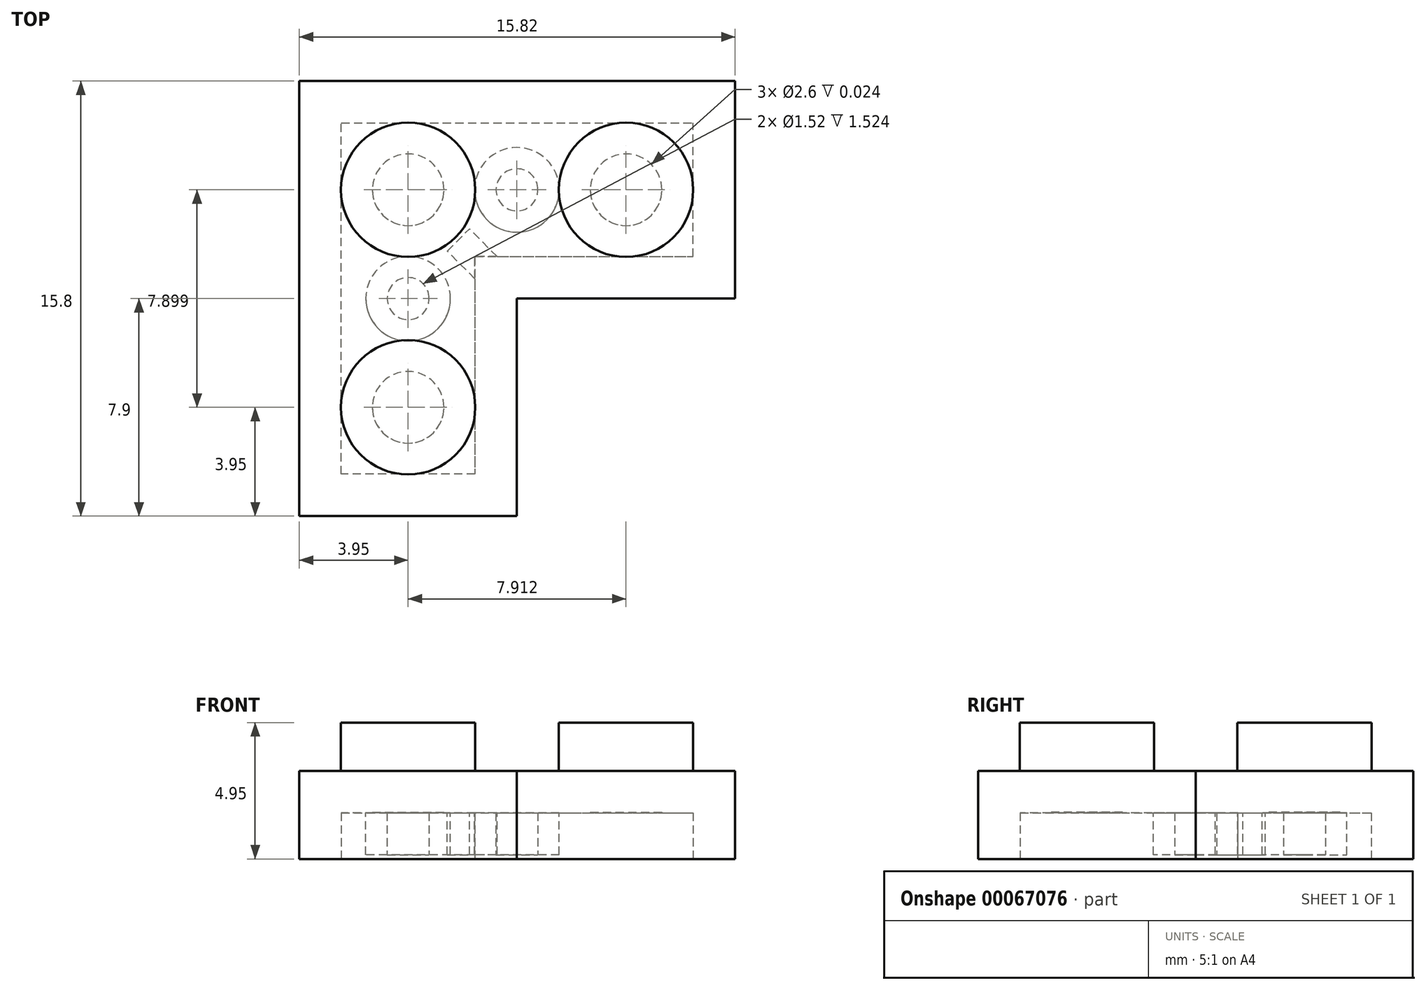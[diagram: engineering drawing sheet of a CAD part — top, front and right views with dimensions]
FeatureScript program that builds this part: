
annotation { "Feature Type Name" : "Feature", "Feature Type Description" : "" }
export const myFeature = defineFeature(function(context is Context, id is Id, definition is map)
    precondition{}
    {
        {
            var Q0;
            Q0=qCreatedBy(makeId("Top.planeOp"),FACE);
            var sketch = newSketch(context, id + "F0", { "sketchPlane" : qUnion([Q0])});
            skLineSegment(sketch, "E0.top", {"start": v(0, -7.9) * mm, "end": v(-7.9, -7.9) * mm});
            skLineSegment(sketch, "E0.left", {"start": v(0, 0) * mm, "end": v(0, -7.9) * mm});
            skLineSegment(sketch, "E0.right", {"start": v(-7.9, 0) * mm, "end": v(-7.9, -7.9) * mm});
            skLineSegment(sketch, "E1.bottom", {"start": v(0, 0) * mm, "end": v(7.92, 0) * mm});
            skLineSegment(sketch, "E1.top", {"start": v(-7.9, 7.9) * mm, "end": v(7.92, 7.9) * mm});
            skLineSegment(sketch, "E1.left", {"start": v(-7.9, 0) * mm, "end": v(-7.9, 7.9) * mm});
            skLineSegment(sketch, "E1.right", {"start": v(7.92, 0) * mm, "end": v(7.92, 7.9) * mm});
            skSolve(sketch);
        }
        {
            var Q0;
            Q0 = qSketchRegion(id + "F0", true);
            extrude(context, id + "F1", {"entities" : qUnion([Q0]), "depth" : 3.2 * mm});
        }
        {
            var Q0;
            Q0=makeQuery(id+"F1.opExtrude","CAP_FACE",FACE,{"disambiguationData":[OSD([sQuery(id+"F0.wireOp",EDGE,"E0.top"),sQuery(id+"F0.wireOp",EDGE,"E0.left"),sQuery(id+"F0.wireOp",EDGE,"E0.right"),sQuery(id+"F0.wireOp",EDGE,"E1.bottom"),sQuery(id+"F0.wireOp",EDGE,"E1.top"),sQuery(id+"F0.wireOp",EDGE,"E1.left"),sQuery(id+"F0.wireOp",EDGE,"E1.right")])],"isStart":true});
            shell(context, id + "F2", {"entities" : qUnion([Q0]), "thickness" : 1.52 * mm});
        }
        {
            var Q0;
            Q0=makeQuery(id+"F1.opExtrude","CAP_FACE",FACE,{"disambiguationData":[OSD([sQuery(id+"F0.wireOp",EDGE,"E0.top"),sQuery(id+"F0.wireOp",EDGE,"E0.left"),sQuery(id+"F0.wireOp",EDGE,"E0.right"),sQuery(id+"F0.wireOp",EDGE,"E1.bottom"),sQuery(id+"F0.wireOp",EDGE,"E1.top"),sQuery(id+"F0.wireOp",EDGE,"E1.left"),sQuery(id+"F0.wireOp",EDGE,"E1.right")])],"isStart":false});
            var sketch = newSketch(context, id + "F3", { "sketchPlane" : qUnion([Q0])});
            skCircle(sketch, "E2", {"center": v(3.96, 3.95) * mm, "radius": 2.44 * mm});
            skCircle(sketch, "E3", {"center": v(-3.95, 3.95) * mm, "radius": 2.44 * mm});
            skCircle(sketch, "E4", {"center": v(-3.95, -3.95) * mm, "radius": 2.44 * mm});
            skSolve(sketch);
        }
        {
            var Q0;
            Q0 = qSketchRegion(id + "F3", true);
            extrude(context, id + "F4", {"entities" : qUnion([Q0]), "operationType" : NewBodyOperationType.ADD, "depth" : 1.75 * mm});
        }
        {
            var Q0;
            Q0=makeQuery(id+"F1.opExtrude","CAP_FACE",FACE,{"disambiguationData":[OSD([sQuery(id+"F0.wireOp",EDGE,"E0.top"),sQuery(id+"F0.wireOp",EDGE,"E0.left"),sQuery(id+"F0.wireOp",EDGE,"E0.right"),sQuery(id+"F0.wireOp",EDGE,"E1.bottom"),sQuery(id+"F0.wireOp",EDGE,"E1.top"),sQuery(id+"F0.wireOp",EDGE,"E1.left"),sQuery(id+"F0.wireOp",EDGE,"E1.right")])],"isStart":true});
            var sketch = newSketch(context, id + "F5", { "sketchPlane" : qUnion([Q0])});
            skCircle(sketch, "E5", {"center": v(-3.95, 3.95) * mm, "radius": 1.3 * mm});
            skCircle(sketch, "E6", {"center": v(-3.95, -3.95) * mm, "radius": 1.3 * mm});
            skCircle(sketch, "E7", {"center": v(3.96, -3.95) * mm, "radius": 1.3 * mm});
            skSolve(sketch);
        }
        {
            var Q0;
            Q0 = qSketchRegion(id + "F5", true);
            extrude(context, id + "F6", {"entities" : qUnion([Q0]), "operationType" : NewBodyOperationType.REMOVE, "oppositeDirection" : true, "depth" : 1.7 * mm});
        }
        {
            var Q0;
            Q0=makeQuery(id+"F2.opShell","OFFSET_FACE",FACE,{"disambiguationData":[OSD([sQuery(id+"F0.wireOp",EDGE,"E0.top"),sQuery(id+"F0.wireOp",EDGE,"E0.left"),sQuery(id+"F0.wireOp",EDGE,"E0.right"),sQuery(id+"F0.wireOp",EDGE,"E1.bottom"),sQuery(id+"F0.wireOp",EDGE,"E1.top"),sQuery(id+"F0.wireOp",EDGE,"E1.left"),sQuery(id+"F0.wireOp",EDGE,"E1.right")])]});
            var sketch = newSketch(context, id + "F7", { "sketchPlane" : qUnion([Q0])});
            skLineSegment(sketch, "E8", {"start": v(-1.52, -0.72) * mm, "end": v(-0.72, -1.52) * mm});
            skLineSegment(sketch, "E9", {"start": v(-1.52, -0.72) * mm, "end": v(-2.53, -1.72) * mm});
            skLineSegment(sketch, "E10", {"start": v(-0.72, -1.52) * mm, "end": v(-1.72, -2.53) * mm});
            skLineSegment(sketch, "E11", {"start": v(-2.53, -1.72) * mm, "end": v(-1.72, -2.53) * mm});
            skSolve(sketch);
        }
        {
            var Q0;
            Q0 = qSketchRegion(id + "F7", true);
            extrude(context, id + "F8", {"entities" : qUnion([Q0]), "operationType" : NewBodyOperationType.ADD, "depth" : 1.52 * mm});
        }
        {
            var Q0;
            Q0=makeQuery(id+"F2.opShell","OFFSET_FACE",FACE,{"disambiguationData":[OSD([sQuery(id+"F0.wireOp",EDGE,"E0.top"),sQuery(id+"F0.wireOp",EDGE,"E0.left"),sQuery(id+"F0.wireOp",EDGE,"E0.right"),sQuery(id+"F0.wireOp",EDGE,"E1.bottom"),sQuery(id+"F0.wireOp",EDGE,"E1.top"),sQuery(id+"F0.wireOp",EDGE,"E1.left"),sQuery(id+"F0.wireOp",EDGE,"E1.right")])]});
            var sketch = newSketch(context, id + "F9", { "sketchPlane" : qUnion([Q0])});
            skCircle(sketch, "E12", {"center": v(-3.95, 0) * mm, "radius": 1.54 * mm});
            skCircle(sketch, "E13", {"center": v(0, -3.95) * mm, "radius": 1.54 * mm});
            skPoint(sketch, "E13.centerSnap0", {"position": v(0.01, -3.95) * mm});
            skSolve(sketch);
        }
        {
            var Q0;
            Q0 = qSketchRegion(id + "F9", true);
            extrude(context, id + "F10", {"entities" : qUnion([Q0]), "operationType" : NewBodyOperationType.ADD, "depth" : 1.52 * mm});
        }
        {
            var Q0;
            Q0=makeQuery(id+"F10.opExtrude","CAP_FACE",FACE,{"disambiguationData":[OSD([sQuery(id+"F9.wireOp",EDGE,"E12")])],"isStart":false});
            var sketch = newSketch(context, id + "F11", { "sketchPlane" : qUnion([Q0])});
            skCircle(sketch, "E14", {"center": v(-3.95, 0) * mm, "radius": 0.76 * mm});
            skSolve(sketch);
        }
        {
            var Q0;
            Q0 = qSketchRegion(id + "F11", true);
            extrude(context, id + "F12", {"entities" : qUnion([Q0]), "operationType" : NewBodyOperationType.REMOVE, "oppositeDirection" : true, "depth" : 1.52 * mm});
        }
        {
            var Q0;
            Q0=makeQuery(id+"F10.opExtrude","CAP_FACE",FACE,{"disambiguationData":[OSD([sQuery(id+"F9.wireOp",EDGE,"E13")])],"isStart":false});
            var sketch = newSketch(context, id + "F13", { "sketchPlane" : qUnion([Q0])});
            skCircle(sketch, "E15", {"center": v(0, -3.95) * mm, "radius": 0.76 * mm});
            skSolve(sketch);
        }
        {
            var Q0;
            Q0 = qSketchRegion(id + "F13", true);
            extrude(context, id + "F14", {"entities" : qUnion([Q0]), "operationType" : NewBodyOperationType.REMOVE, "oppositeDirection" : true, "depth" : 1.52 * mm});
        }
    });
